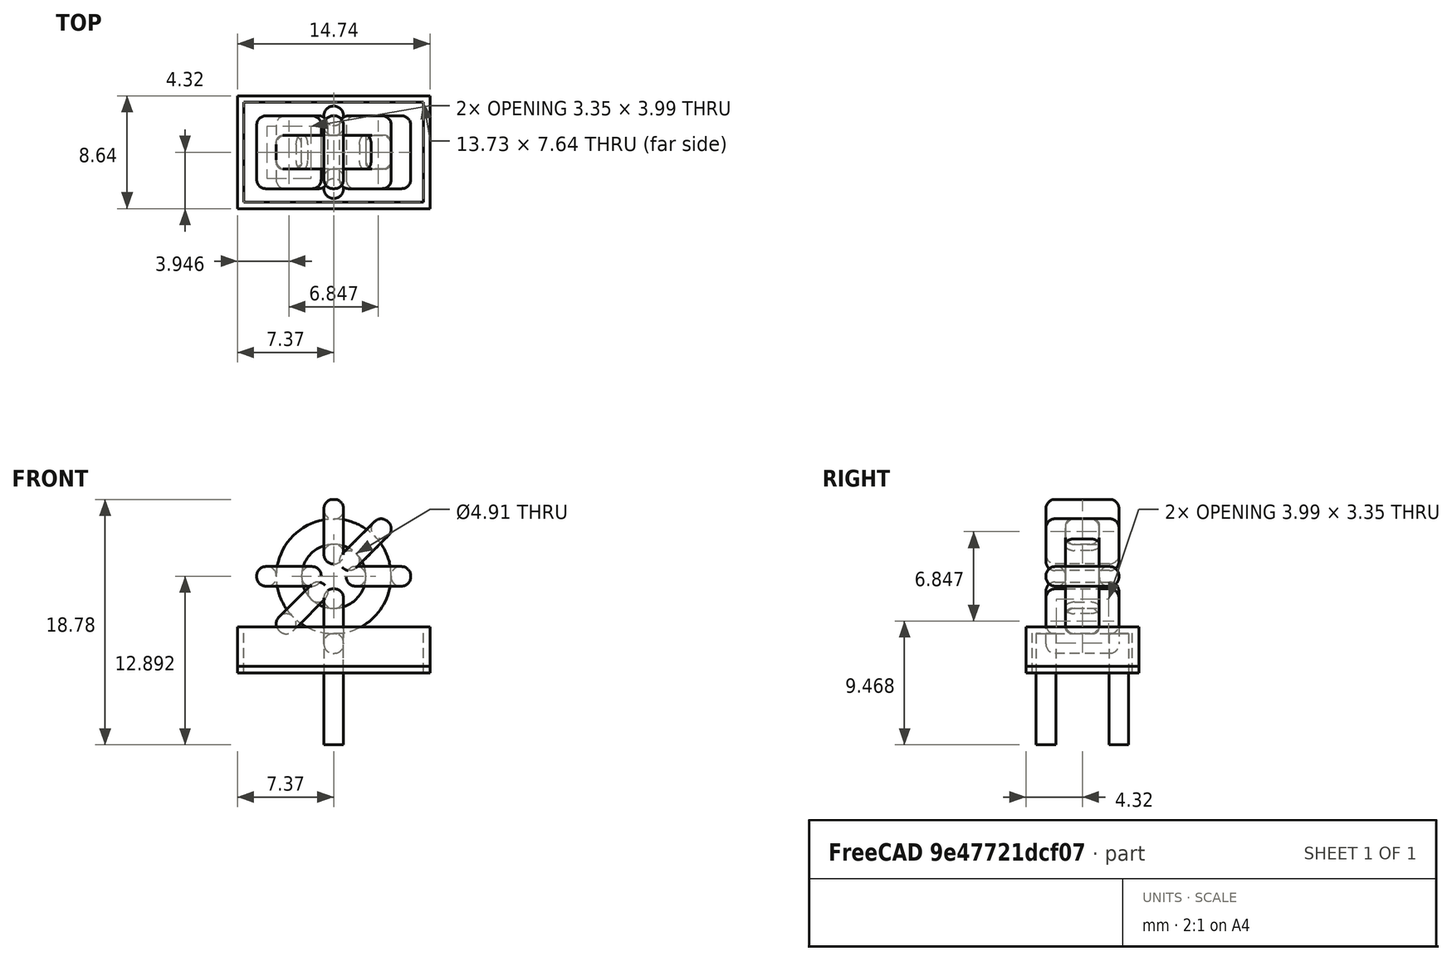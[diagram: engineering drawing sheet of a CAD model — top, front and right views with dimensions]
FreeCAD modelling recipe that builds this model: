
FCSTD DOCUMENT  (FreeCAD 0.16R6703 (Git))
Label: L_Radial_round_toroid_vertical_box_master
License: All rights reserved
LicenseURL: http://en.wikipedia.org/wiki/All_rights_reserved
objects: Sketcher::SketchObject×8, PartDesign::Pad×8, PartDesign::Fillet×5, Spreadsheet::Sheet×1
note: 29 computed .brp shape members not serialized (recipe doc carries the construction recipe); baked Part::Feature solids carry a one-line shape summary decoded from their .brp

FEATURE [Spreadsheet::Sheet] Spreadsheet  label="dimensions"
  cells = A1=Wx; B1(Wx)=11.784; C1(WW)=4.91; D1(iWx)=14.73; A2=Wy; B2(Wy)=5.58; D2(iWy)=8.640000000000001; A3=RM; B3(RMx)=5.58; C3(RMy)=0; A4=d_wire; B4(d_wire)=1.5; A5=H; B5(H)=14.73; A6=offsetx; B6(offsetx)=7.365
FEATURE [Sketcher::SketchObject] Sketch
  Placement = pos=(0,-2.79,0) rot=(1,0,0;1.5708rad)
  expr: Placement.Base.y = -Spreadsheet.RMx / 2
  expr: Constraints[0] = Spreadsheet.Wx / 2 - Spreadsheet.d_wire
  expr: Constraints[4] = Spreadsheet.WW / 2
  expr: Constraints[2] = Spreadsheet.Wx / 2 + Spreadsheet.d_wire + 0.5
  sketch-geometry (2):
    g0: Circle CenterX=0 CenterY=7.892 CenterZ=0 NormalX=0 NormalY=0 NormalZ=1 Radius=4.392
    g1: Circle CenterX=0 CenterY=7.892 CenterZ=0 NormalX=0 NormalY=0 NormalZ=1 Radius=2.455
  constraints (5):
    c: Radius(g0) = 4.392
    c: DistanceX(g-1,g0) = 0
    c: DistanceY(g-1,g0) = 7.892
    c: Coincident(g1,g0)
    c: Radius(g1) = 2.455
FEATURE [PartDesign::Pad] Pad
  Length = 2.58
  Length2 = 100
  Midplane = true
  Placement = pos=(0,-2.79,0) rot=(1,0,0;1.5708rad)
  Sketch = -> Sketch
  Type = 0
  expr: Length = Spreadsheet.Wy - 2 * Spreadsheet.d_wire
FEATURE [Sketcher::SketchObject] Sketch001
  Placement = pos=(0,0,2) rot=(0,0,1;0rad)
  expr: Placement.Base.z = 0.5 + Spreadsheet.d_wire
  expr: Constraints[4] = Spreadsheet.RMy
  expr: Constraints[2] = -Spreadsheet.RMx
  expr: Constraints[1] = Spreadsheet.d_wire / 2
  sketch-geometry (2):
    g0: Circle CenterX=0 CenterY=0 CenterZ=0 NormalX=0 NormalY=0 NormalZ=1 Radius=0.75
    g1: Circle CenterX=0 CenterY=-5.58 CenterZ=0 NormalX=0 NormalY=0 NormalZ=1 Radius=0.75
  constraints (5):
    c: Equal(g0,g1)
    c: Radius(g0) = 0.75
    c: DistanceY(g-1,g1) = -5.58
    c: Coincident(g0,g-1)
    c: DistanceX(g-1,g1) = 0
FEATURE [PartDesign::Pad] Pad001
  Length = 1.5
  Length2 = 7
  Placement = pos=(0,0,2) rot=(0,0,1;0rad)
  Reversed = true
  Sketch = -> Sketch001
  Type = 4
  expr: Length2 = 5.5 + Spreadsheet.d_wire
  expr: Length = Spreadsheet.d_wire
FEATURE [PartDesign::Fillet] Fillet
  Base = -> Pad [Edge6,Edge3,Edge2]
  Placement = pos=(0,-2.79,0) rot=(1,0,0;1.5708rad)
  Radius = 0.5
FEATURE [Sketcher::SketchObject] Sketch003
  Placement = pos=(0,0,7.892) rot=(1,0,0;3.14159rad)
  expr: Constraints[18] = Spreadsheet.d_wire
  expr: Constraints[16] = Spreadsheet.d_wire
  expr: Constraints[19] = Spreadsheet.d_wire
  expr: Constraints[17] = Spreadsheet.d_wire
  expr: Placement.Base.y = -1 * (Spreadsheet.RMx - Spreadsheet.Wy) / 2
  expr: Constraints[21] = (Spreadsheet.Wx - Spreadsheet.WW) / 2 - Spreadsheet.d_wire
  expr: Constraints[22] = Spreadsheet.Wx / 2 - Spreadsheet.d_wire
  expr: Constraints[43] = Spreadsheet.d_wire
  expr: Constraints[48] = Spreadsheet.Wx - Spreadsheet.d_wire * 2
  expr: Constraints[49] = Spreadsheet.Wy
  expr: Placement.Base.z = Spreadsheet.Wx / 2 + Spreadsheet.d_wire + 0.5
  sketch-geometry (16):
    g0: LineSegment StartX=-0.955 StartY=0 StartZ=0 EndX=-5.892 EndY=0 EndZ=0
    g1: LineSegment StartX=-5.892 StartY=0 StartZ=0 EndX=-5.892 EndY=5.58 EndZ=0
    g2: LineSegment StartX=-5.892 StartY=5.58 StartZ=0 EndX=-0.955 EndY=5.58 EndZ=0
    g3: LineSegment StartX=-0.955 StartY=5.58 StartZ=0 EndX=-0.955 EndY=0 EndZ=0
    g4: LineSegment StartX=-4.392 StartY=4.08 StartZ=0 EndX=-2.455 EndY=4.08 EndZ=0
    g5: LineSegment StartX=-2.455 StartY=4.08 StartZ=0 EndX=-2.455 EndY=1.5 EndZ=0
    g6: LineSegment StartX=-2.455 StartY=1.5 StartZ=0 EndX=-4.392 EndY=1.5 EndZ=0
    g7: LineSegment StartX=-4.392 StartY=1.5 StartZ=0 EndX=-4.392 EndY=4.08 EndZ=0
    g8: LineSegment StartX=0.955 StartY=5.58 StartZ=0 EndX=5.892 EndY=5.58 EndZ=0
    g9: LineSegment StartX=5.892 StartY=5.58 StartZ=0 EndX=5.892 EndY=0 EndZ=0
    g10: LineSegment StartX=5.892 StartY=0 StartZ=0 EndX=0.955 EndY=0 EndZ=0
    g11: LineSegment StartX=0.955 StartY=0 StartZ=0 EndX=0.955 EndY=5.58 EndZ=0
    g12: LineSegment StartX=2.455 StartY=4.08 StartZ=0 EndX=4.392 EndY=4.08 EndZ=0
    g13: LineSegment StartX=4.392 StartY=4.08 StartZ=0 EndX=4.392 EndY=1.5 EndZ=0
    g14: LineSegment StartX=4.392 StartY=1.5 StartZ=0 EndX=2.455 EndY=1.5 EndZ=0
    g15: LineSegment StartX=2.455 StartY=1.5 StartZ=0 EndX=2.455 EndY=4.08 EndZ=0
  constraints (50):
    c: Horizontal(g0)
    c: Coincident(g1,g0)
    c: Vertical(g1)
    c: Coincident(g2,g1)
    c: Horizontal(g2)
    c: Coincident(g3,g2)
    c: Coincident(g3,g0)
    c: Vertical(g3)
    c: Coincident(g4,g5)
    c: Coincident(g5,g6)
    c: Coincident(g6,g7)
    c: Coincident(g7,g4)
    c: Horizontal(g4)
    c: Horizontal(g6)
    c: Vertical(g5)
    c: Vertical(g7)
    c: DistanceX(g1,g4) = 1.5
    c: DistanceY(g4,g1) = 1.5
    c: DistanceX(g5,g0) = 1.5
    c: DistanceY(g0,g5) = 1.5
    c: DistanceY(g-1,g0) = 0
    c: DistanceX(g6,g6) = 1.937
    c: DistanceX(g6,g-1) = 4.392
    c: Coincident(g8,g9)
    c: Coincident(g9,g10)
    c: Coincident(g10,g11)
    c: Coincident(g11,g8)
    c: Horizontal(g8)
    c: Horizontal(g10)
    c: Vertical(g9)
    c: Vertical(g11)
    c: Coincident(g12,g13)
    c: Coincident(g13,g14)
    c: Coincident(g14,g15)
    c: Coincident(g15,g12)
    c: Horizontal(g12)
    c: Horizontal(g14)
    c: Vertical(g13)
    c: Vertical(g15)
    c: DistanceY(g8,g2) = 0
    c: DistanceY(g10,g0) = 0
    c: DistanceY(g14,g5) = 0
    c: DistanceY(g12,g4) = 0
    c: DistanceX(g8,g12) = 1.5
    c: Equal(g8,g2)
    c: Equal(g12,g4)
    c: Equal(g9,g1)
    c: Equal(g13,g7)
    c: DistanceX(g4,g12) = 8.784
    c: DistanceY(g0,g1) = 5.58
FEATURE [PartDesign::Pad] Pad002
  Length = 1.5
  Length2 = 100
  Midplane = true
  Placement = pos=(0,0,7.892) rot=(1,0,0;3.14159rad)
  Sketch = -> Sketch003
  Type = 0
  expr: Length = Spreadsheet.d_wire
FEATURE [PartDesign::Fillet] Fillet001
  Base = -> Pad002 [Edge38,Edge41,Edge42,Edge43,Edge29,Edge32,Edge33,Edge34,Edge25,Edge35,Edge36,Edge13,Edge14,Edge15,Edge16,Edge17,Edge18,Edge19,Edge1,Edge2,Edge3,Edge4,Edge5,Edge6,Edge7,Edge37,Edge39,Edge40,Edge20,Edge23,Edge24,Edge21,Edge22,Edge8,Edge9,Edge10,Edge11,Edge12,Edge26,Edge27,+8 more]
  Placement = pos=(0,0,7.892) rot=(1,0,0;3.14159rad)
  Radius = 0.705
  expr: Radius = Spreadsheet.d_wire * 0.47
FEATURE [Sketcher::SketchObject] Sketch004
  Placement = pos=(0,0,7.892) rot=(0.92388,0,0.382683;3.14159rad)
  expr: Constraints[18] = Spreadsheet.d_wire
  expr: Constraints[16] = Spreadsheet.d_wire
  expr: Constraints[19] = Spreadsheet.d_wire
  expr: Constraints[17] = Spreadsheet.d_wire
  expr: Placement.Base.y = -1 * (Spreadsheet.RMx - Spreadsheet.Wy) / 2
  expr: Constraints[21] = (Spreadsheet.Wx - Spreadsheet.WW) / 2 - Spreadsheet.d_wire
  expr: Constraints[22] = Spreadsheet.Wx / 2 - Spreadsheet.d_wire
  expr: Constraints[43] = Spreadsheet.d_wire
  expr: Constraints[48] = Spreadsheet.Wx - 2 * Spreadsheet.d_wire
  expr: Constraints[49] = Spreadsheet.Wy
  expr: Placement.Base.z = Spreadsheet.Wx / 2 + Spreadsheet.d_wire + 0.5
  sketch-geometry (16):
    g0: LineSegment StartX=-0.955 StartY=0 StartZ=0 EndX=-5.892 EndY=0 EndZ=0
    g1: LineSegment StartX=-5.892 StartY=0 StartZ=0 EndX=-5.892 EndY=5.58 EndZ=0
    g2: LineSegment StartX=-5.892 StartY=5.58 StartZ=0 EndX=-0.955 EndY=5.58 EndZ=0
    g3: LineSegment StartX=-0.955 StartY=5.58 StartZ=0 EndX=-0.955 EndY=0 EndZ=0
    g4: LineSegment StartX=-4.392 StartY=4.08 StartZ=0 EndX=-2.455 EndY=4.08 EndZ=0
    g5: LineSegment StartX=-2.455 StartY=4.08 StartZ=0 EndX=-2.455 EndY=1.5 EndZ=0
    g6: LineSegment StartX=-2.455 StartY=1.5 StartZ=0 EndX=-4.392 EndY=1.5 EndZ=0
    g7: LineSegment StartX=-4.392 StartY=1.5 StartZ=0 EndX=-4.392 EndY=4.08 EndZ=0
    g8: LineSegment StartX=0.955 StartY=5.58 StartZ=0 EndX=5.892 EndY=5.58 EndZ=0
    g9: LineSegment StartX=5.892 StartY=5.58 StartZ=0 EndX=5.892 EndY=0 EndZ=0
    g10: LineSegment StartX=5.892 StartY=0 StartZ=0 EndX=0.955 EndY=0 EndZ=0
    g11: LineSegment StartX=0.955 StartY=0 StartZ=0 EndX=0.955 EndY=5.58 EndZ=0
    g12: LineSegment StartX=2.455 StartY=4.08 StartZ=0 EndX=4.392 EndY=4.08 EndZ=0
    g13: LineSegment StartX=4.392 StartY=4.08 StartZ=0 EndX=4.392 EndY=1.5 EndZ=0
    g14: LineSegment StartX=4.392 StartY=1.5 StartZ=0 EndX=2.455 EndY=1.5 EndZ=0
    g15: LineSegment StartX=2.455 StartY=1.5 StartZ=0 EndX=2.455 EndY=4.08 EndZ=0
  constraints (50):
    c: Horizontal(g0)
    c: Coincident(g1,g0)
    c: Vertical(g1)
    c: Coincident(g2,g1)
    c: Horizontal(g2)
    c: Coincident(g3,g2)
    c: Coincident(g3,g0)
    c: Vertical(g3)
    c: Coincident(g4,g5)
    c: Coincident(g5,g6)
    c: Coincident(g6,g7)
    c: Coincident(g7,g4)
    c: Horizontal(g4)
    c: Horizontal(g6)
    c: Vertical(g5)
    c: Vertical(g7)
    c: DistanceX(g1,g4) = 1.5
    c: DistanceY(g4,g1) = 1.5
    c: DistanceX(g5,g0) = 1.5
    c: DistanceY(g0,g5) = 1.5
    c: DistanceY(g-1,g0) = 0
    c: DistanceX(g6,g6) = 1.937
    c: DistanceX(g6,g-1) = 4.392
    c: Coincident(g8,g9)
    c: Coincident(g9,g10)
    c: Coincident(g10,g11)
    c: Coincident(g11,g8)
    c: Horizontal(g8)
    c: Horizontal(g10)
    c: Vertical(g9)
    c: Vertical(g11)
    c: Coincident(g12,g13)
    c: Coincident(g13,g14)
    c: Coincident(g14,g15)
    c: Coincident(g15,g12)
    c: Horizontal(g12)
    c: Horizontal(g14)
    c: Vertical(g13)
    c: Vertical(g15)
    c: DistanceY(g8,g2) = 0
    c: DistanceY(g10,g0) = 0
    c: DistanceY(g14,g5) = 0
    c: DistanceY(g12,g4) = 0
    c: DistanceX(g8,g12) = 1.5
    c: Equal(g8,g2)
    c: Equal(g12,g4)
    c: Equal(g9,g1)
    c: Equal(g13,g7)
    c: DistanceX(g4,g12) = 8.784
    c: DistanceY(g0,g1) = 5.58
FEATURE [PartDesign::Pad] Pad003
  Length = 1.5
  Length2 = 100
  Midplane = true
  Placement = pos=(0,0,7.892) rot=(0.92388,0,0.382683;3.14159rad)
  Sketch = -> Sketch004
  Type = 0
  expr: Length = Spreadsheet.d_wire
FEATURE [PartDesign::Fillet] Fillet002
  Base = -> Pad003 [Edge38,Edge41,Edge42,Edge43,Edge29,Edge32,Edge33,Edge34,Edge25,Edge35,Edge36,Edge13,Edge14,Edge15,Edge16,Edge17,Edge18,Edge19,Edge1,Edge2,Edge3,Edge4,Edge5,Edge6,Edge7,Edge37,Edge39,Edge40,Edge20,Edge23,Edge24,Edge21,Edge22,Edge8,Edge9,Edge10,Edge11,Edge12,Edge26,Edge27,+8 more]
  Placement = pos=(0,0,7.892) rot=(0.92388,0,0.382683;3.14159rad)
  Radius = 0.705
  expr: Radius = Spreadsheet.d_wire * 0.47
FEATURE [Sketcher::SketchObject] Sketch005
  Placement = pos=(0,0,7.892) rot=(0.92388,0,-0.382683;3.14159rad)
  expr: Constraints[18] = Spreadsheet.d_wire
  expr: Constraints[16] = Spreadsheet.d_wire
  expr: Constraints[19] = Spreadsheet.d_wire
  expr: Constraints[17] = Spreadsheet.d_wire
  expr: Placement.Base.y = -1 * (Spreadsheet.RMx - Spreadsheet.Wy) / 2
  expr: Constraints[21] = (Spreadsheet.Wx - Spreadsheet.WW) / 2 - Spreadsheet.d_wire
  expr: Constraints[22] = Spreadsheet.Wx / 2 - Spreadsheet.d_wire
  expr: Constraints[43] = Spreadsheet.d_wire
  expr: Constraints[48] = Spreadsheet.Wx - 2 * Spreadsheet.d_wire
  expr: Constraints[49] = Spreadsheet.Wy
  expr: Placement.Base.z = Spreadsheet.Wx / 2 + Spreadsheet.d_wire + 0.5
  sketch-geometry (16):
    g0: LineSegment StartX=-0.955 StartY=0 StartZ=0 EndX=-5.892 EndY=0 EndZ=0
    g1: LineSegment StartX=-5.892 StartY=0 StartZ=0 EndX=-5.892 EndY=5.58 EndZ=0
    g2: LineSegment StartX=-5.892 StartY=5.58 StartZ=0 EndX=-0.955 EndY=5.58 EndZ=0
    g3: LineSegment StartX=-0.955 StartY=5.58 StartZ=0 EndX=-0.955 EndY=0 EndZ=0
    g4: LineSegment StartX=-4.392 StartY=4.08 StartZ=0 EndX=-2.455 EndY=4.08 EndZ=0
    g5: LineSegment StartX=-2.455 StartY=4.08 StartZ=0 EndX=-2.455 EndY=1.5 EndZ=0
    g6: LineSegment StartX=-2.455 StartY=1.5 StartZ=0 EndX=-4.392 EndY=1.5 EndZ=0
    g7: LineSegment StartX=-4.392 StartY=1.5 StartZ=0 EndX=-4.392 EndY=4.08 EndZ=0
    g8: LineSegment StartX=0.955 StartY=5.58 StartZ=0 EndX=5.892 EndY=5.58 EndZ=0
    g9: LineSegment StartX=5.892 StartY=5.58 StartZ=0 EndX=5.892 EndY=0 EndZ=0
    g10: LineSegment StartX=5.892 StartY=0 StartZ=0 EndX=0.955 EndY=0 EndZ=0
    g11: LineSegment StartX=0.955 StartY=0 StartZ=0 EndX=0.955 EndY=5.58 EndZ=0
    g12: LineSegment StartX=2.455 StartY=4.08 StartZ=0 EndX=4.392 EndY=4.08 EndZ=0
    g13: LineSegment StartX=4.392 StartY=4.08 StartZ=0 EndX=4.392 EndY=1.5 EndZ=0
    g14: LineSegment StartX=4.392 StartY=1.5 StartZ=0 EndX=2.455 EndY=1.5 EndZ=0
    g15: LineSegment StartX=2.455 StartY=1.5 StartZ=0 EndX=2.455 EndY=4.08 EndZ=0
  constraints (50):
    c: Horizontal(g0)
    c: Coincident(g1,g0)
    c: Vertical(g1)
    c: Coincident(g2,g1)
    c: Horizontal(g2)
    c: Coincident(g3,g2)
    c: Coincident(g3,g0)
    c: Vertical(g3)
    c: Coincident(g4,g5)
    c: Coincident(g5,g6)
    c: Coincident(g6,g7)
    c: Coincident(g7,g4)
    c: Horizontal(g4)
    c: Horizontal(g6)
    c: Vertical(g5)
    c: Vertical(g7)
    c: DistanceX(g1,g4) = 1.5
    c: DistanceY(g4,g1) = 1.5
    c: DistanceX(g5,g0) = 1.5
    c: DistanceY(g0,g5) = 1.5
    c: DistanceY(g-1,g0) = 0
    c: DistanceX(g6,g6) = 1.937
    c: DistanceX(g6,g-1) = 4.392
    c: Coincident(g8,g9)
    c: Coincident(g9,g10)
    c: Coincident(g10,g11)
    c: Coincident(g11,g8)
    c: Horizontal(g8)
    c: Horizontal(g10)
    c: Vertical(g9)
    c: Vertical(g11)
    c: Coincident(g12,g13)
    c: Coincident(g13,g14)
    c: Coincident(g14,g15)
    c: Coincident(g15,g12)
    c: Horizontal(g12)
    c: Horizontal(g14)
    c: Vertical(g13)
    c: Vertical(g15)
    c: DistanceY(g8,g2) = 0
    c: DistanceY(g10,g0) = 0
    c: DistanceY(g14,g5) = 0
    c: DistanceY(g12,g4) = 0
    c: DistanceX(g8,g12) = 1.5
    c: Equal(g8,g2)
    c: Equal(g12,g4)
    c: Equal(g9,g1)
    c: Equal(g13,g7)
    c: DistanceX(g4,g12) = 8.784
    c: DistanceY(g0,g1) = 5.58
FEATURE [PartDesign::Pad] Pad004
  Length = 1.5
  Length2 = 100
  Midplane = true
  Placement = pos=(0,0,7.892) rot=(0.92388,0,-0.382683;3.14159rad)
  Sketch = -> Sketch005
  Type = 0
  expr: Length = Spreadsheet.d_wire
FEATURE [PartDesign::Fillet] Fillet003
  Base = -> Pad004 [Edge38,Edge41,Edge42,Edge43,Edge29,Edge32,Edge33,Edge34,Edge25,Edge35,Edge36,Edge13,Edge14,Edge15,Edge16,Edge17,Edge18,Edge19,Edge1,Edge2,Edge3,Edge4,Edge5,Edge6,Edge7,Edge37,Edge39,Edge40,Edge20,Edge23,Edge24,Edge21,Edge22,Edge8,Edge9,Edge10,Edge11,Edge12,Edge26,Edge27,+8 more]
  Placement = pos=(0,0,7.892) rot=(0.92388,0,-0.382683;3.14159rad)
  Radius = 0.705
  expr: Radius = Spreadsheet.d_wire * 0.47
FEATURE [Sketcher::SketchObject] Sketch006
  Placement = pos=(0,0,7.892) rot=(0.707107,0,0.707107;3.14159rad)
  expr: Constraints[18] = Spreadsheet.d_wire
  expr: Constraints[16] = Spreadsheet.d_wire
  expr: Constraints[19] = Spreadsheet.d_wire
  expr: Constraints[17] = Spreadsheet.d_wire
  expr: Placement.Base.y = -1 * (Spreadsheet.RMx - Spreadsheet.Wy) / 2
  expr: Constraints[21] = (Spreadsheet.Wx - Spreadsheet.WW) / 2 - Spreadsheet.d_wire
  expr: Constraints[22] = Spreadsheet.Wx / 2 - Spreadsheet.d_wire
  expr: Constraints[43] = Spreadsheet.d_wire
  expr: Constraints[48] = Spreadsheet.Wx - Spreadsheet.d_wire * 2
  expr: Constraints[49] = Spreadsheet.Wy
  expr: Placement.Base.z = Spreadsheet.Wx / 2 + Spreadsheet.d_wire + 0.5
  sketch-geometry (16):
    g0: LineSegment StartX=-0.955 StartY=0 StartZ=0 EndX=-5.892 EndY=0 EndZ=0
    g1: LineSegment StartX=-5.892 StartY=0 StartZ=0 EndX=-5.892 EndY=5.58 EndZ=0
    g2: LineSegment StartX=-5.892 StartY=5.58 StartZ=0 EndX=-0.955 EndY=5.58 EndZ=0
    g3: LineSegment StartX=-0.955 StartY=5.58 StartZ=0 EndX=-0.955 EndY=0 EndZ=0
    g4: LineSegment StartX=-4.392 StartY=4.08 StartZ=0 EndX=-2.455 EndY=4.08 EndZ=0
    g5: LineSegment StartX=-2.455 StartY=4.08 StartZ=0 EndX=-2.455 EndY=1.5 EndZ=0
    g6: LineSegment StartX=-2.455 StartY=1.5 StartZ=0 EndX=-4.392 EndY=1.5 EndZ=0
    g7: LineSegment StartX=-4.392 StartY=1.5 StartZ=0 EndX=-4.392 EndY=4.08 EndZ=0
    g8: LineSegment StartX=0.955 StartY=5.58 StartZ=0 EndX=5.892 EndY=5.58 EndZ=0
    g9: LineSegment StartX=5.892 StartY=5.58 StartZ=0 EndX=5.892 EndY=0 EndZ=0
    g10: LineSegment StartX=5.892 StartY=0 StartZ=0 EndX=0.955 EndY=0 EndZ=0
    g11: LineSegment StartX=0.955 StartY=0 StartZ=0 EndX=0.955 EndY=5.58 EndZ=0
    g12: LineSegment StartX=2.455 StartY=4.08 StartZ=0 EndX=4.392 EndY=4.08 EndZ=0
    g13: LineSegment StartX=4.392 StartY=4.08 StartZ=0 EndX=4.392 EndY=1.5 EndZ=0
    g14: LineSegment StartX=4.392 StartY=1.5 StartZ=0 EndX=2.455 EndY=1.5 EndZ=0
    g15: LineSegment StartX=2.455 StartY=1.5 StartZ=0 EndX=2.455 EndY=4.08 EndZ=0
  constraints (50):
    c: Horizontal(g0)
    c: Coincident(g1,g0)
    c: Vertical(g1)
    c: Coincident(g2,g1)
    c: Horizontal(g2)
    c: Coincident(g3,g2)
    c: Coincident(g3,g0)
    c: Vertical(g3)
    c: Coincident(g4,g5)
    c: Coincident(g5,g6)
    c: Coincident(g6,g7)
    c: Coincident(g7,g4)
    c: Horizontal(g4)
    c: Horizontal(g6)
    c: Vertical(g5)
    c: Vertical(g7)
    c: DistanceX(g1,g4) = 1.5
    c: DistanceY(g4,g1) = 1.5
    c: DistanceX(g5,g0) = 1.5
    c: DistanceY(g0,g5) = 1.5
    c: DistanceY(g-1,g0) = 0
    c: DistanceX(g6,g6) = 1.937
    c: DistanceX(g6,g-1) = 4.392
    c: Coincident(g8,g9)
    c: Coincident(g9,g10)
    c: Coincident(g10,g11)
    c: Coincident(g11,g8)
    c: Horizontal(g8)
    c: Horizontal(g10)
    c: Vertical(g9)
    c: Vertical(g11)
    c: Coincident(g12,g13)
    c: Coincident(g13,g14)
    c: Coincident(g14,g15)
    c: Coincident(g15,g12)
    c: Horizontal(g12)
    c: Horizontal(g14)
    c: Vertical(g13)
    c: Vertical(g15)
    c: DistanceY(g8,g2) = 0
    c: DistanceY(g10,g0) = 0
    c: DistanceY(g14,g5) = 0
    c: DistanceY(g12,g4) = 0
    c: DistanceX(g8,g12) = 1.5
    c: Equal(g8,g2)
    c: Equal(g12,g4)
    c: Equal(g9,g1)
    c: Equal(g13,g7)
    c: DistanceX(g4,g12) = 8.784
    c: DistanceY(g0,g1) = 5.58
FEATURE [PartDesign::Pad] Pad005
  Length = 1.5
  Length2 = 100
  Midplane = true
  Placement = pos=(0,0,7.892) rot=(0.707107,0,0.707107;3.14159rad)
  Sketch = -> Sketch006
  Type = 0
  expr: Length = Spreadsheet.d_wire
FEATURE [PartDesign::Fillet] Fillet004
  Base = -> Pad005 [Edge38,Edge41,Edge42,Edge43,Edge29,Edge32,Edge33,Edge34,Edge25,Edge35,Edge36,Edge13,Edge14,Edge15,Edge16,Edge17,Edge18,Edge19,Edge1,Edge2,Edge3,Edge4,Edge5,Edge6,Edge7,Edge37,Edge39,Edge40,Edge20,Edge23,Edge24,Edge21,Edge22,Edge8,Edge9,Edge10,Edge11,Edge12,Edge26,Edge27,+8 more]
  Placement = pos=(0,0,7.892) rot=(0.707107,0,0.707107;3.14159rad)
  Radius = 0.705
  expr: Radius = Spreadsheet.d_wire * 0.47
FEATURE [Sketcher::SketchObject] Sketch007
  Placement = pos=(0,0,0.5) rot=(0,0,1;0rad)
  expr: Placement.Base.z = 0.5
  expr: Constraints[11] = Spreadsheet.iWx / 2
  expr: Constraints[10] = (Spreadsheet.iWy - Spreadsheet.RMx) / 2
  expr: Constraints[9] = Spreadsheet.iWy
  expr: Constraints[8] = Spreadsheet.iWx
  sketch-geometry (4):
    g0: LineSegment StartX=-7.365 StartY=1.53 StartZ=0 EndX=7.365 EndY=1.53 EndZ=0
    g1: LineSegment StartX=7.365 StartY=1.53 StartZ=0 EndX=7.365 EndY=-7.11 EndZ=0
    g2: LineSegment StartX=7.365 StartY=-7.11 StartZ=0 EndX=-7.365 EndY=-7.11 EndZ=0
    g3: LineSegment StartX=-7.365 StartY=-7.11 StartZ=0 EndX=-7.365 EndY=1.53 EndZ=0
  constraints (12):
    c: Coincident(g0,g1)
    c: Coincident(g1,g2)
    c: Coincident(g2,g3)
    c: Coincident(g3,g0)
    c: Horizontal(g0)
    c: Horizontal(g2)
    c: Vertical(g1)
    c: Vertical(g3)
    c: DistanceX(g0,g0) = 14.73
    c: DistanceY(g3,g3) = 8.64
    c: DistanceY(g-1,g0) = 1.53
    c: DistanceX(g0,g-1) = 7.365
FEATURE [PartDesign::Pad] Pad006
  Length = 0.5
  Length2 = 100
  Placement = pos=(0,0,0.5) rot=(0,0,1;0rad)
  Sketch = -> Sketch007
  Type = 0
FEATURE [Sketcher::SketchObject] Sketch008
  Placement = pos=(0,0,0.5) rot=(0,0,1;0rad)
  expr: Constraints[8] = Spreadsheet.iWx
  expr: Constraints[9] = Spreadsheet.iWy
  expr: Constraints[10] = (Spreadsheet.iWy - Spreadsheet.RMx) / 2
  expr: Placement.Base.z = 0.5
  expr: Constraints[21] = 0.5
  expr: Constraints[11] = Spreadsheet.iWx / 2
  sketch-geometry (8):
    g0: LineSegment StartX=-7.365 StartY=1.53 StartZ=0 EndX=7.365 EndY=1.53 EndZ=0
    g1: LineSegment StartX=7.365 StartY=1.53 StartZ=0 EndX=7.365 EndY=-7.11 EndZ=0
    g2: LineSegment StartX=7.365 StartY=-7.11 StartZ=0 EndX=-7.365 EndY=-7.11 EndZ=0
    g3: LineSegment StartX=-7.365 StartY=-7.11 StartZ=0 EndX=-7.365 EndY=1.53 EndZ=0
    g4: LineSegment StartX=-6.865 StartY=1.03 StartZ=0 EndX=6.865 EndY=1.03 EndZ=0
    g5: LineSegment StartX=6.865 StartY=1.03 StartZ=0 EndX=6.865 EndY=-6.61 EndZ=0
    g6: LineSegment StartX=6.865 StartY=-6.61 StartZ=0 EndX=-6.865 EndY=-6.61 EndZ=0
    g7: LineSegment StartX=-6.865 StartY=-6.61 StartZ=0 EndX=-6.865 EndY=1.03 EndZ=0
  constraints (24):
    c: Coincident(g0,g1)
    c: Coincident(g1,g2)
    c: Coincident(g2,g3)
    c: Coincident(g3,g0)
    c: Horizontal(g0)
    c: Horizontal(g2)
    c: Vertical(g1)
    c: Vertical(g3)
    c: DistanceX(g0,g0) = 14.73
    c: DistanceY(g3,g3) = 8.64
    c: DistanceY(g-1,g0) = 1.53
    c: DistanceX(g0,g-1) = 7.365
    c: Coincident(g4,g5)
    c: Coincident(g5,g6)
    c: Coincident(g6,g7)
    c: Coincident(g7,g4)
    c: Horizontal(g4)
    c: Horizontal(g6)
    c: Vertical(g5)
    c: Vertical(g7)
    c: DistanceX(g5,g1) = 0.5
    c: DistanceY(g1,g5) = 0.5
    c: DistanceX(g0,g4) = 0.5
    c: DistanceY(g4,g0) = 0.5
FEATURE [PartDesign::Pad] Pad007
  Length = 3.5352
  Length2 = 100
  Placement = pos=(0,0,0.5) rot=(0,0,1;0rad)
  Sketch = -> Sketch008
  Type = 0
  expr: Length = Spreadsheet.Wx * 0.3
